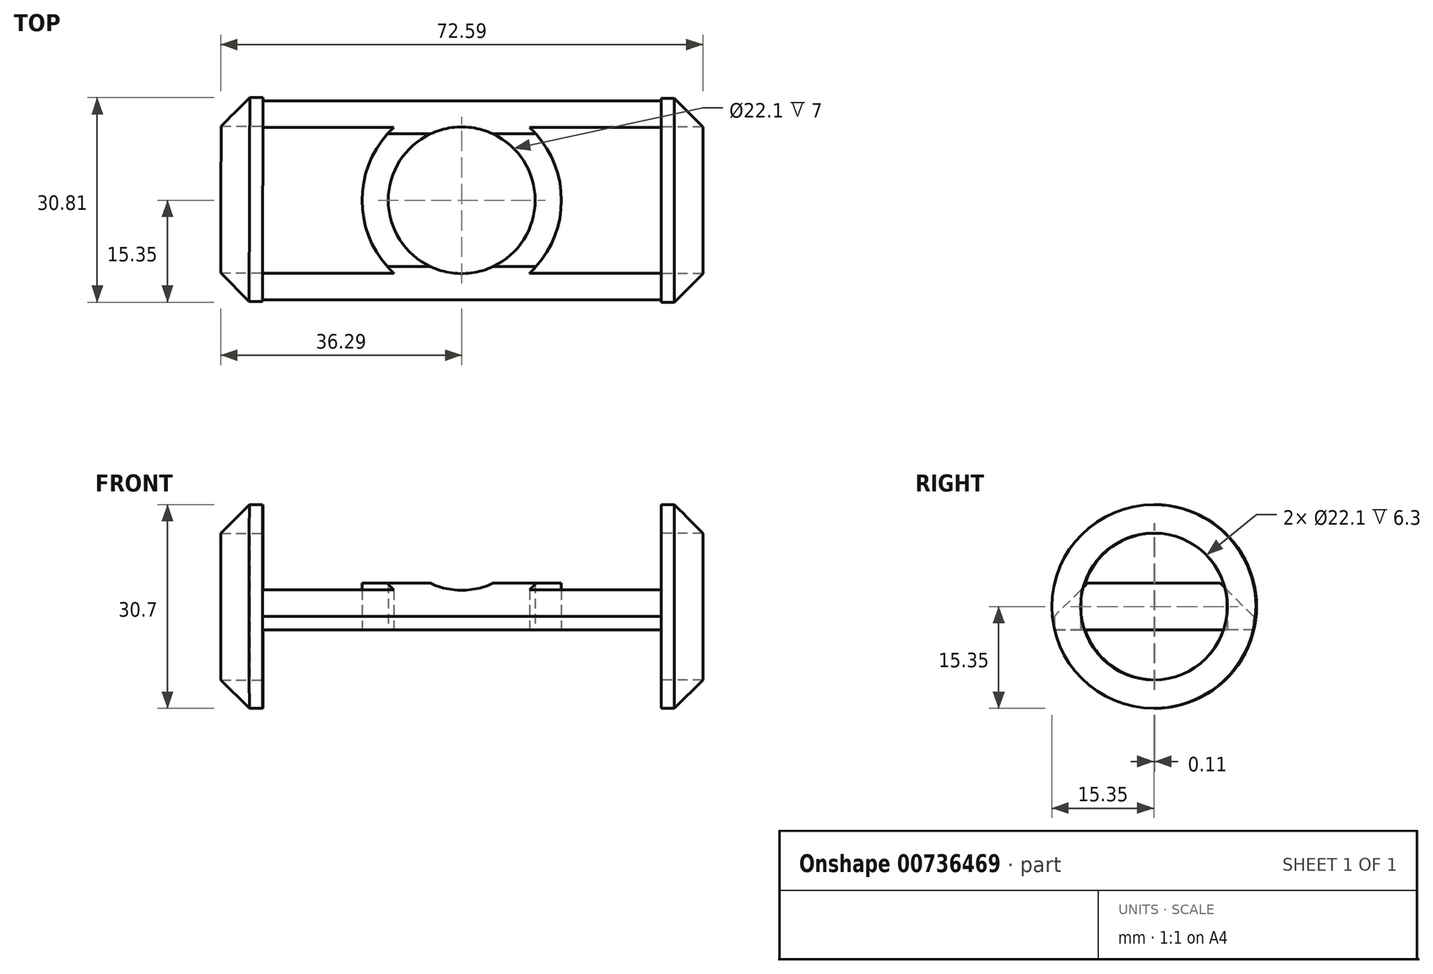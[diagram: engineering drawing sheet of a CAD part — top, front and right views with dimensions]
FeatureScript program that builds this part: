
annotation { "Feature Type Name" : "Feature", "Feature Type Description" : "" }
export const myFeature = defineFeature(function(context is Context, id is Id, definition is map)
    precondition{}
    {
        {
            var Q0;
            Q0=qCreatedBy(makeId("Top.planeOp"),FACE);
            var sketch = newSketch(context, id + "F0", { "sketchPlane" : qUnion([Q0])});
            skCircle(sketch, "E0", {"center": v(0, 0) * mm, "radius": 11.05 * mm});
            skCircle(sketch, "E1", {"center": v(0, 0) * mm, "radius": 15 * mm});
            skLineSegment(sketch, "E2", {"start": v(0, 15) * mm, "end": v(0, -15) * mm, "construction": true});
            skLineSegment(sketch, "E3", {"start": v(0, 15) * mm, "end": v(-30, 15) * mm});
            skLineSegment(sketch, "E4", {"start": v(0, -15) * mm, "end": v(-30, -15) * mm});
            skLineSegment(sketch, "E5", {"start": v(-10.2, 11) * mm, "end": v(-29.99, 11) * mm});
            skLineSegment(sketch, "E6", {"start": v(-10.2, -11) * mm, "end": v(-29.99, -11) * mm});
            skLineSegment(sketch, "E7", {"start": v(-30, -15) * mm, "end": v(-29.99, -11) * mm});
            skLineSegment(sketch, "E8", {"start": v(-29.99, 11) * mm, "end": v(-30, 15) * mm});
            skLineSegment(sketch, "E9", {"start": v(0, 15) * mm, "end": v(30, 15) * mm});
            skLineSegment(sketch, "E10", {"start": v(0, -15) * mm, "end": v(30, -15) * mm});
            skLineSegment(sketch, "E11", {"start": v(-30, 0) * mm, "end": v(-30, 15) * mm, "construction": true});
            skLineSegment(sketch, "E12", {"start": v(-30, 0) * mm, "end": v(-30, -15) * mm, "construction": true});
            skLineSegment(sketch, "E13", {"start": v(0, 0) * mm, "end": v(30, 0) * mm, "construction": true});
            skLineSegment(sketch, "E14", {"start": v(30, 0) * mm, "end": v(30, -15) * mm, "construction": true});
            skLineSegment(sketch, "E15", {"start": v(30, 0) * mm, "end": v(30, 15) * mm, "construction": true});
            skLineSegment(sketch, "E16", {"start": v(10.2, 11) * mm, "end": v(30, 11) * mm});
            skLineSegment(sketch, "E17", {"start": v(30, 15) * mm, "end": v(30, 11) * mm});
            skLineSegment(sketch, "E18", {"start": v(10.2, -11) * mm, "end": v(30, -11) * mm});
            skLineSegment(sketch, "E19", {"start": v(30, -11) * mm, "end": v(30, -15) * mm});
            skSolve(sketch);
        }
        {
            var Q0;
            Q0=qSketchRegion(id+"F0",true);
            extrude(context, id + "F1", {"entities" : qUnion([Q0]), "depth" : 7 * mm, "offsetDistance" : 25 * mm});
        }
        {
            var Q0;
            Q0=makeQuery(id+"F1.opExtrude","SWEPT_FACE",FACE,{"disambiguationData":[OSD([sQuery(id+"F0.wireOp",EDGE,"E7")])]});
            var sketch = newSketch(context, id + "F2", { "sketchPlane" : qUnion([Q0])});
            skLineSegment(sketch, "E20", {"start": v(0, 0) * mm, "end": v(0, 3.5) * mm, "construction": true});
            skCircle(sketch, "E21", {"center": v(0, 3.5) * mm, "radius": 11.05 * mm});
            skCircle(sketch, "E22", {"center": v(0, 3.5) * mm, "radius": 15.35 * mm});
            skSolve(sketch);
        }
        {
            var Q0;
            Q0=qSketchRegion(id+"F2",true);
            extrude(context, id + "F3", {"entities" : qUnion([Q0]), "operationType" : NewBodyOperationType.ADD, "depth" : 7 * mm, "offsetDistance" : 25 * mm});
        }
        {
            var Q0;
            Q0=makeQuery(id+"F1.opExtrude","SWEPT_FACE",FACE,{"disambiguationData":[OSD([sQuery(id+"F0.wireOp",EDGE,"E17")])]});
            var sketch = newSketch(context, id + "F4", { "sketchPlane" : qUnion([Q0])});
            skLineSegment(sketch, "E23", {"start": v(0, 0) * mm, "end": v(0, 3.5) * mm, "construction": true});
            skCircle(sketch, "E24", {"center": v(0, 3.5) * mm, "radius": 11.05 * mm});
            skCircle(sketch, "E25", {"center": v(0, 3.5) * mm, "radius": 15.35 * mm});
            skSolve(sketch);
        }
        {
            var Q0;
            Q0=qSketchRegion(id+"F4",true);
            extrude(context, id + "F5", {"entities" : qUnion([Q0]), "operationType" : NewBodyOperationType.ADD, "depth" : 7 * mm, "offsetDistance" : 25 * mm});
        }
        {
            var Q0;
            Q0=makeQuery(id+"F1.opExtrude","CAP_EDGE",EDGE,{"disambiguationData":[OSD([sQuery(id+"F0.wireOp",EDGE,"E3"),sQuery(id+"F0.wireOp",EDGE,"E9")])],"isStart":false});
            var Q1;
            Q1=makeQuery(id+"F1.opExtrude","CAP_EDGE",EDGE,{"disambiguationData":[OSD([sQuery(id+"F0.wireOp",EDGE,"E4"),sQuery(id+"F0.wireOp",EDGE,"E10")])],"isStart":false});
            var Q2;
            Q2=makeQuery(id+"F5.opExtrude","CAP_EDGE",EDGE,{"disambiguationData":[OSD([sQuery(id+"F4.wireOp",EDGE,"E25")])],"isStart":false});
            var Q3;
            Q3=makeQuery(id+"F3.opExtrude","CAP_EDGE",EDGE,{"disambiguationData":[OSD([sQuery(id+"F2.wireOp",EDGE,"E22")])],"isStart":false});
            chamfer(context, id + "F6", {"entities" : qUnion([Q0, Q1, Q2, Q3]), "width" : 5 * mm, "tangentPropagation" : true});
        }
    });
